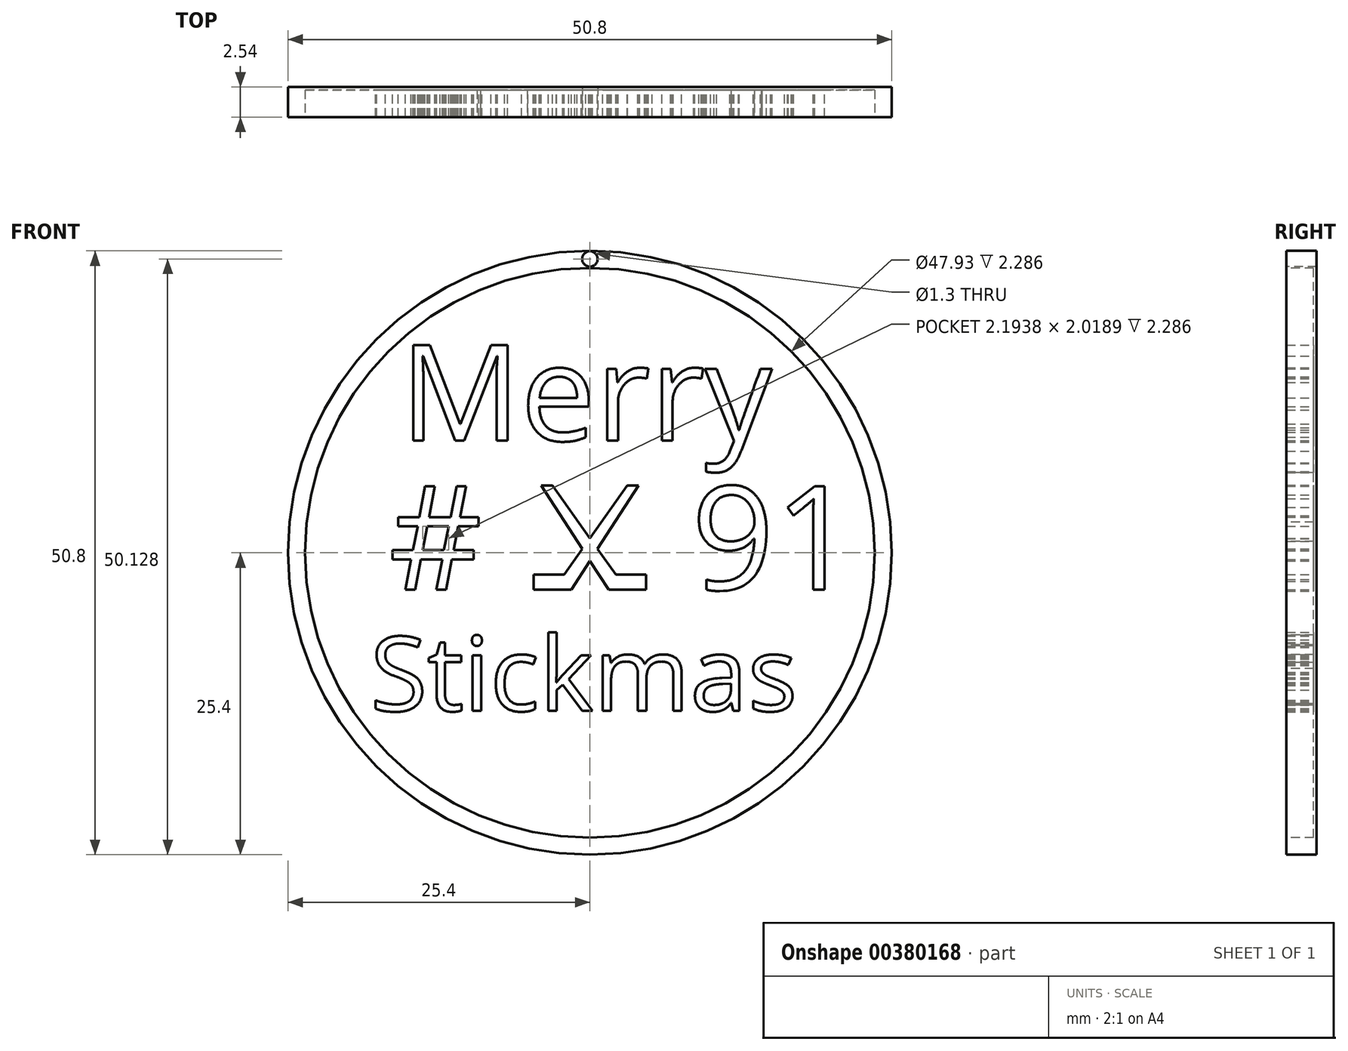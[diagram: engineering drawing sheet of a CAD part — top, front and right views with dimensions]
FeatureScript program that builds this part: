
annotation { "Feature Type Name" : "Feature", "Feature Type Description" : "" }
export const myFeature = defineFeature(function(context is Context, id is Id, definition is map)
    precondition{}
    {
        {
            var Q0;
            Q0=qCreatedBy(makeId("Front.planeOp"),FACE);
            var sketch = newSketch(context, id + "F0", { "sketchPlane" : qUnion([Q0])});
            skCircle(sketch, "E0", {"center": v(0, 0) * mm, "radius": 25.4 * mm});
            skSolve(sketch);
        }
        {
            var Q0;
            Q0=makeQuery(id+"F0.imprint","IMPRINT",FACE,{"disambiguationData":[TD([[makeQuery(id+"F0.imprint","IMPRINT",EDGE,{"derivedFrom":sQuery(id+"F0.wireOp",EDGE,"E0")}),1.0]])]});
            extrude(context, id + "F1", {"entities" : qUnion([Q0]), "depth" : 2.54 * mm});
        }
        {
            var Q0;
            Q0=makeQuery(id+"F1.opExtrude","CAP_FACE",FACE,{"disambiguationData":[OSD([sQuery(id+"F0.wireOp",EDGE,"E0")])],"isStart":false});
            var sketch = newSketch(context, id + "F2", { "sketchPlane" : qUnion([Q0])});
            skCircle(sketch, "E1", {"center": v(0, 0) * mm, "radius": 23.97 * mm});
            skSolve(sketch);
        }
        {
            var Q0;
            Q0=makeQuery(id+"F2.imprint","IMPRINT",FACE,{"disambiguationData":[TD([[makeQuery(id+"F2.imprint","IMPRINT",EDGE,{"derivedFrom":sQuery(id+"F2.wireOp",EDGE,"E1")}),1.0]])]});
            extrude(context, id + "F3", {"entities" : qUnion([Q0]), "operationType" : NewBodyOperationType.REMOVE, "oppositeDirection" : true, "depth" : 2.3 * mm});
        }
        {
            var Q0;
            Q0=makeQuery(id+"F3.boolean.opBoolean","COPY",FACE,{"derivedFrom":makeQuery(id+"F3.opExtrude","CAP_FACE",FACE,{"disambiguationData":[OSD([sQuery(id+"F2.wireOp",EDGE,"E1")])],"isStart":false})});
            var sketch = newSketch(context, id + "F4", { "sketchPlane" : qUnion([Q0])});
            skText(sketch, "E2", { "text": "Merry", "fontName": "OpenSans-Regular.ttf"});
            skText(sketch, "E3", { "text": "Stickmas", "fontName": "OpenSans-Regular.ttf"});
            skLineSegment(sketch, "E4", {"start": v(-4.1, 5.66) * mm, "end": v(-0.65, 0.32) * mm});
            skLineSegment(sketch, "E5", {"start": v(1.57, -3.11) * mm, "end": v(4.74, -3.11) * mm});
            skLineSegment(sketch, "E6", {"start": v(4.74, -3.11) * mm, "end": v(4.74, -1.83) * mm});
            skLineSegment(sketch, "E7", {"start": v(4.74, -1.83) * mm, "end": v(2.18, -1.83) * mm});
            skLineSegment(sketch, "E8", {"start": v(2.18, -1.83) * mm, "end": v(0.65, 0.32) * mm});
            skLineSegment(sketch, "E9", {"start": v(-3.16, 5.66) * mm, "end": v(-4.1, 5.66) * mm});
            skLineSegment(sketch, "E10.MirrorCS", {"start": v(-2.18, -1.83) * mm, "end": v(-0.65, 0.32) * mm});
            skLineSegment(sketch, "E11.MirrorCS", {"start": v(4.1, 5.66) * mm, "end": v(0.65, 0.32) * mm});
            skLineSegment(sketch, "E12.MirrorCS", {"start": v(-1.57, -3.11) * mm, "end": v(-4.74, -3.11) * mm});
            skLineSegment(sketch, "E13.MirrorCS", {"start": v(-4.74, -1.83) * mm, "end": v(-2.18, -1.83) * mm});
            skLineSegment(sketch, "E14.MirrorCS", {"start": v(-4.74, -3.11) * mm, "end": v(-4.74, -1.83) * mm});
            skLineSegment(sketch, "E15.MirrorCS", {"start": v(3.16, 5.66) * mm, "end": v(4.1, 5.66) * mm});
            skLineSegment(sketch, "E16.trimOffspring", {"start": v(0, 1.23) * mm, "end": v(-3.16, 5.66) * mm});
            skLineSegment(sketch, "E17.trimOffspring", {"start": v(0, 1.23) * mm, "end": v(3.16, 5.66) * mm});
            skLineSegment(sketch, "E18.trimOffspring", {"start": v(0, -0.68) * mm, "end": v(1.57, -3.11) * mm});
            skLineSegment(sketch, "E19.trimOffspring", {"start": v(0, -0.68) * mm, "end": v(-1.57, -3.11) * mm});
            const initialGuessF4  = {"E2": [-0.01598, 0.00944, 1, 0, 0.0081], "E3": [-0.01848, -0.0133, 1, 0, 0.00628]};
            skSetInitialGuess(sketch, initialGuessF4);
            skSolve(sketch);
        }
        {
            var Q0;
            Q0 = qSketchRegion(id + "F4", true);
            var Q1;
            Q1=makeQuery(id+"F1.opExtrude","CAP_FACE",FACE,{"disambiguationData":[OSD([sQuery(id+"F0.wireOp",EDGE,"E0")])],"isStart":false});
            extrude(context, id + "F5", {"entities" : qUnion([Q0]), "operationType" : NewBodyOperationType.ADD, "endBound" : BoundingType.UP_TO_SURFACE, "endBoundEntityFace" : qUnion([Q1]), "depth" : 2.54 * mm});
        }
        {
            var Q0;
            {var subQ0=sQuery(id+"F2.wireOp",EDGE,"E1");Q0=makeQuery(id+"F5.boolean.opBoolean","SPLIT",FACE,{"disambiguationData":[TD([makeQuery(id+"F3.boolean.opBoolean","COPY",FACE,{"derivedFrom":makeQuery(id+"F3.opExtrude","SWEPT_FACE",FACE,{"disambiguationData":[OSD([subQ0])]})})])],"derivedFrom":makeQuery(id+"F3.boolean.opBoolean","COPY",FACE,{"derivedFrom":makeQuery(id+"F3.opExtrude","CAP_FACE",FACE,{"disambiguationData":[OSD([subQ0])],"isStart":false})})});}
            var sketch = newSketch(context, id + "F6", { "sketchPlane" : qUnion([Q0])});
            skText(sketch, "E20", { "text": "#", "fontName": "OpenSans-Regular.ttf"});
            skText(sketch, "E21", { "text": "91", "fontName": "OpenSans-Regular.ttf"});
            const initialGuessF6  = {"E20": [-0.0169, -0.0031, 1, 0, 0.00876], "E21": [0.00855, -0.0031, 1, 0, 0.00876]};
            skSetInitialGuess(sketch, initialGuessF6);
            skSolve(sketch);
        }
        {
            var Q0;
            Q0 = qSketchRegion(id + "F6", true);
            var Q1;
            Q1=makeQuery(id+"F1.opExtrude","CAP_FACE",FACE,{"disambiguationData":[OSD([sQuery(id+"F0.wireOp",EDGE,"E0")])],"isStart":false});
            extrude(context, id + "F7", {"entities" : qUnion([Q0]), "operationType" : NewBodyOperationType.ADD, "endBound" : BoundingType.UP_TO_SURFACE, "endBoundEntityFace" : qUnion([Q1]), "depth" : 25.4 * mm});
        }
        {
            var Q0;
            Q0=makeQuery(id+"F1.opExtrude","CAP_FACE",FACE,{"disambiguationData":[OSD([sQuery(id+"F0.wireOp",EDGE,"E0")])],"isStart":false});
            var sketch = newSketch(context, id + "F8", { "sketchPlane" : qUnion([Q0])});
            skCircle(sketch, "E22", {"center": v(0, 24.73) * mm, "radius": 0.65 * mm});
            skSolve(sketch);
        }
        {
            var Q0;
            Q0 = qSketchRegion(id + "F8", true);
            extrude(context, id + "F9", {"entities" : qUnion([Q0]), "operationType" : NewBodyOperationType.REMOVE, "endBound" : BoundingType.THROUGH_ALL, "oppositeDirection" : true, "depth" : 25.4 * mm});
        }
    });
